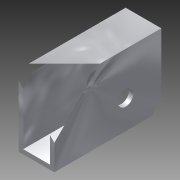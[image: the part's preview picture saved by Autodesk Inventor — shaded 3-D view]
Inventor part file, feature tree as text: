
AUTODESK INVENTOR PART (.ipt)
format: ipt  version: 2015 SP1 (Build 190203100, 203)  size: 118,272 bytes
history: native  units: in
note: dims shown in document units (in); Inventor stores cm internally (conversion verified against a paired STEP export)
features: sketch x2, extrude x1, hole x1
ambient origin geometry x8: Origin, YZ Plane, XZ Plane, XY Plane, X Axis, Y Axis, Z Axis, Center Point
bodies: Solid1 (feature_tree)
feature tree (4):
  extrude  "Extrusion1"  Depth=2.0in
  hole  "Hole1"  [1 undecoded]
  sketch  "Sketch1"  dims[d0=1.0in d1=2.0in]
  sketch  "Sketch2"  dims[d2=0.75in d3=1.75in d4=0.125in d5=0.125in d6=3.0in d7=0.0in d8=0.8125in d9=1.0in d10=0.4375in d11=0.75in d12=0.375in d13=0.25in d14=0.5635in d15=1.0in d16=0.8108in d17=1.0in d18=1.0in]
note: 1 required parameter value undecoded (feature->parameter linkage not recoverable at this tier; creation-order binding heuristic only, values carry confidence <= 0.55)
